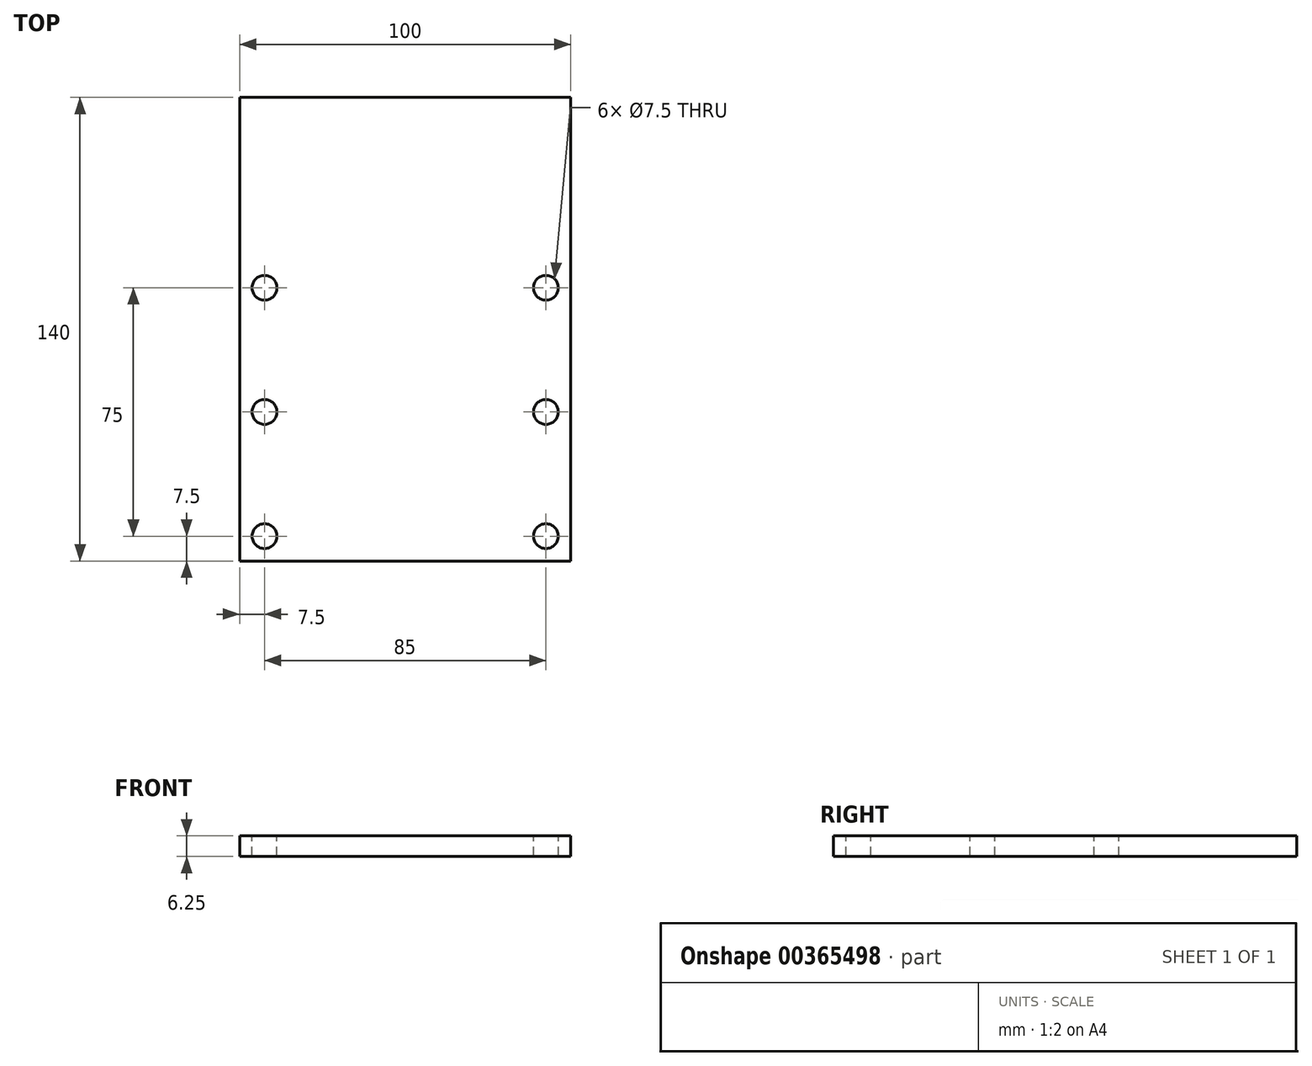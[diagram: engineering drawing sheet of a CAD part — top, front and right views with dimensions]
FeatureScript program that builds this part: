
annotation { "Feature Type Name" : "Feature", "Feature Type Description" : "" }
export const myFeature = defineFeature(function(context is Context, id is Id, definition is map)
    precondition{}
    {
        {
            var Q0;
            Q0=qCreatedBy(makeId("Top.planeOp"),FACE);
            var sketch = newSketch(context, id + "F0", { "sketchPlane" : qUnion([Q0])});
            skLineSegment(sketch, "E0.bottom", {"start": v(50, 70) * mm, "end": v(-50, 70) * mm});
            skLineSegment(sketch, "E0.top", {"start": v(50, -70) * mm, "end": v(-50, -70) * mm});
            skLineSegment(sketch, "E0.left", {"start": v(50, 70) * mm, "end": v(50, -70) * mm});
            skLineSegment(sketch, "E0.right", {"start": v(-50, 70) * mm, "end": v(-50, -70) * mm});
            skPoint(sketch, "E0.middle", {"position": v(0, 0) * mm});
            skSolve(sketch);
        }
        {
            var Q0;
            Q0 = qSketchRegion(id + "F0", true);
            extrude(context, id + "F1", {"entities" : qUnion([Q0]), "depth" : 6.25 * mm});
        }
        {
            var Q0;
            Q0=makeQuery(id+"F1.opExtrude","CAP_FACE",FACE,{"disambiguationData":[OSD([sQuery(id+"F0.wireOp",EDGE,"E0.bottom"),sQuery(id+"F0.wireOp",EDGE,"E0.top"),sQuery(id+"F0.wireOp",EDGE,"E0.left"),sQuery(id+"F0.wireOp",EDGE,"E0.right")])],"isStart":false});
            var sketch = newSketch(context, id + "F2", { "sketchPlane" : qUnion([Q0])});
            skCircle(sketch, "E1", {"center": v(-42.5, -62.5) * mm, "radius": 3.75 * mm});
            skCircle(sketch, "E2", {"center": v(-42.5, -25) * mm, "radius": 3.75 * mm});
            skCircle(sketch, "E3", {"center": v(-42.5, 12.5) * mm, "radius": 3.75 * mm});
            skCircle(sketch, "E4", {"center": v(42.5, 12.5) * mm, "radius": 3.75 * mm});
            skCircle(sketch, "E5", {"center": v(42.5, -62.5) * mm, "radius": 3.75 * mm});
            skCircle(sketch, "E6", {"center": v(42.5, -25) * mm, "radius": 3.75 * mm});
            skSolve(sketch);
        }
        {
            var Q0;
            Q0 = qSketchRegion(id + "F2", true);
            extrude(context, id + "F3", {"entities" : qUnion([Q0]), "operationType" : NewBodyOperationType.REMOVE, "oppositeDirection" : true, "depth" : 25 * mm});
        }
    });
